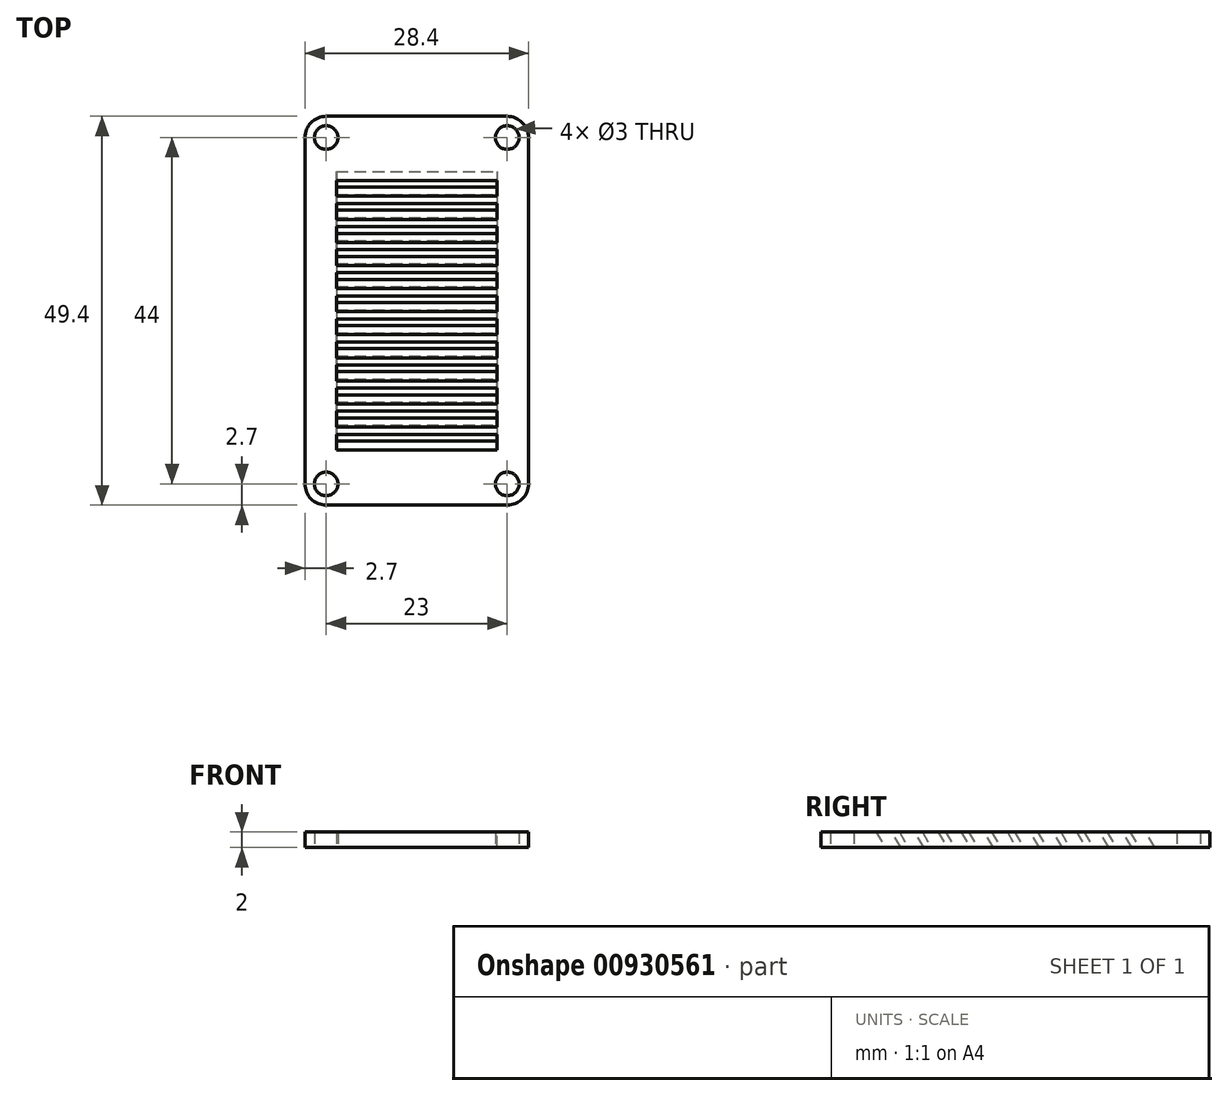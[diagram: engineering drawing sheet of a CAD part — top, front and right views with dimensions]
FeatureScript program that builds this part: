
annotation { "Feature Type Name" : "Feature", "Feature Type Description" : "" }
export const myFeature = defineFeature(function(context is Context, id is Id, definition is map)
    precondition{}
    {
        {
            var Q0;
            Q0=qCreatedBy(makeId("Top.planeOp"),FACE);
            var sketch = newSketch(context, id + "F0", { "sketchPlane" : qUnion([Q0])});
            skLineSegment(sketch, "E0", {"start": v(-14.5, 47) * mm, "end": v(-14.5, 3) * mm, "construction": true});
            skLineSegment(sketch, "E1", {"start": v(-11.5, 0) * mm, "end": v(11.5, 0) * mm, "construction": true});
            skLineSegment(sketch, "E2", {"start": v(14.5, 47) * mm, "end": v(14.5, 3) * mm, "construction": true});
            skLineSegment(sketch, "E3", {"start": v(-11.5, 50) * mm, "end": v(11.5, 50) * mm, "construction": true});
            skArc(sketch, "E4", {"start": v(-11.5, 50) * mm, "mid": v(-13.62, 49.12) * mm, "end": v(-14.5, 47) * mm, "construction": true});
            skArc(sketch, "E5", {"start": v(14.5, 47) * mm, "mid": v(13.62, 49.12) * mm, "end": v(11.5, 50) * mm, "construction": true});
            skArc(sketch, "E6", {"start": v(-14.5, 3) * mm, "mid": v(-13.62, 0.88) * mm, "end": v(-11.5, 0) * mm, "construction": true});
            skArc(sketch, "E7", {"start": v(11.5, 0) * mm, "mid": v(13.62, 0.88) * mm, "end": v(14.5, 3) * mm, "construction": true});
            skLineSegment(sketch, "E8", {"start": v(-14.2, 47) * mm, "end": v(-14.2, 3) * mm});
            skLineSegment(sketch, "E9", {"start": v(-11.5, 49.7) * mm, "end": v(11.5, 49.7) * mm});
            skLineSegment(sketch, "E10", {"start": v(14.2, 47) * mm, "end": v(14.2, 3) * mm});
            skLineSegment(sketch, "E11", {"start": v(-11.5, 0.3) * mm, "end": v(11.5, 0.3) * mm});
            skArc(sketch, "E12", {"start": v(-11.5, 49.7) * mm, "mid": v(-13.4, 48.9) * mm, "end": v(-14.2, 47) * mm});
            skArc(sketch, "E13", {"start": v(14.2, 47) * mm, "mid": v(13.4, 48.9) * mm, "end": v(11.5, 49.7) * mm});
            skArc(sketch, "E14", {"start": v(-14.2, 3) * mm, "mid": v(-13.4, 1.1) * mm, "end": v(-11.5, 0.3) * mm});
            skArc(sketch, "E15", {"start": v(11.5, 0.3) * mm, "mid": v(13.4, 1.1) * mm, "end": v(14.2, 3) * mm});
            skCircle(sketch, "E16", {"center": v(-11.5, 47) * mm, "radius": 1.5 * mm});
            skCircle(sketch, "E17", {"center": v(11.5, 47) * mm, "radius": 1.5 * mm});
            skCircle(sketch, "E18", {"center": v(-11.5, 3) * mm, "radius": 1.5 * mm});
            skCircle(sketch, "E19", {"center": v(11.5, 3) * mm, "radius": 1.5 * mm});
            skLineSegment(sketch, "E20.bottom", {"start": v(-10.2, 42.7) * mm, "end": v(10.2, 42.7) * mm});
            skLineSegment(sketch, "E20.top", {"start": v(-10.2, 7.3) * mm, "end": v(10.2, 7.3) * mm});
            skLineSegment(sketch, "E20.left", {"start": v(-10.2, 42.7) * mm, "end": v(-10.2, 7.3) * mm});
            skLineSegment(sketch, "E20.right", {"start": v(10.2, 42.7) * mm, "end": v(10.2, 7.3) * mm});
            skSolve(sketch);
        }
        {
            var Q0;
            Q0=qSketchRegion(id+"F0",true);
            extrude(context, id + "F1", {"entities" : qUnion([Q0]), "depth" : 2 * mm, "offsetDistance" : 25 * mm});
        }
        {
            var Q0;
            Q0=makeQuery(id+"F1.opExtrude","SWEPT_FACE",FACE,{"disambiguationData":[OSD([sQuery(id+"F0.wireOp",EDGE,"E20.right")])]});
            var sketch = newSketch(context, id + "F2", { "sketchPlane" : qUnion([Q0])});
            skLineSegment(sketch, "E21", {"start": v(-42.7, 1) * mm, "end": v(-7.3, 1) * mm, "construction": true});
            skLineSegment(sketch, "E22", {"start": v(-25, 2) * mm, "end": v(-25, 0) * mm, "construction": true});
            skLineSegment(sketch, "E23", {"start": v(-24.88, 2) * mm, "end": v(-23.96, 2) * mm});
            skLineSegment(sketch, "E24", {"start": v(-23.96, 2) * mm, "end": v(-25.12, 0) * mm});
            skLineSegment(sketch, "E25", {"start": v(-25.12, 0) * mm, "end": v(-26.04, 0) * mm});
            skLineSegment(sketch, "E26", {"start": v(-26.04, 0) * mm, "end": v(-24.88, 2) * mm});
            skLineSegment(sketch, "E27", {"start": v(-25, 2) * mm, "end": v(-24.88, 2) * mm, "construction": true});
            skLineSegment(sketch, "E28", {"start": v(-25, 0) * mm, "end": v(-25.12, 0) * mm, "construction": true});
            skLineSegment(sketch, "E29", {"start": v(-21.95, 2) * mm, "end": v(-23.1, 0) * mm});
            skLineSegment(sketch, "E30", {"start": v(-23.1, 0) * mm, "end": v(-22.18, 0) * mm});
            skLineSegment(sketch, "E31", {"start": v(-22.18, 0) * mm, "end": v(-21.03, 2) * mm});
            skLineSegment(sketch, "E32", {"start": v(-21.03, 2) * mm, "end": v(-21.95, 2) * mm});
            skLineSegment(sketch, "E33", {"start": v(-19.02, 2) * mm, "end": v(-20.18, 0) * mm});
            skLineSegment(sketch, "E34", {"start": v(-20.18, 0) * mm, "end": v(-19.25, 0) * mm});
            skLineSegment(sketch, "E35", {"start": v(-19.25, 0) * mm, "end": v(-18.1, 2) * mm});
            skLineSegment(sketch, "E36", {"start": v(-18.1, 2) * mm, "end": v(-19.02, 2) * mm});
            skLineSegment(sketch, "E37", {"start": v(-16.1, 2) * mm, "end": v(-15.17, 2) * mm});
            skLineSegment(sketch, "E38", {"start": v(-15.17, 2) * mm, "end": v(-16.32, 0) * mm});
            skLineSegment(sketch, "E39", {"start": v(-16.32, 0) * mm, "end": v(-17.25, 0) * mm});
            skLineSegment(sketch, "E40", {"start": v(-17.25, 0) * mm, "end": v(-16.1, 2) * mm});
            skLineSegment(sketch, "E41", {"start": v(-13.16, 2) * mm, "end": v(-14.32, 0) * mm});
            skLineSegment(sketch, "E42", {"start": v(-14.32, 0) * mm, "end": v(-13.4, 0) * mm});
            skLineSegment(sketch, "E43", {"start": v(-13.4, 0) * mm, "end": v(-12.24, 2) * mm});
            skLineSegment(sketch, "E44", {"start": v(-12.24, 2) * mm, "end": v(-13.16, 2) * mm});
            skLineSegment(sketch, "E45", {"start": v(-10.23, 2) * mm, "end": v(-11.39, 0) * mm});
            skLineSegment(sketch, "E46", {"start": v(-11.39, 0) * mm, "end": v(-10.46, 0) * mm});
            skLineSegment(sketch, "E47", {"start": v(-10.46, 0) * mm, "end": v(-9.3, 2) * mm});
            skLineSegment(sketch, "E48", {"start": v(-9.3, 2) * mm, "end": v(-10.23, 2) * mm});
            skLineSegment(sketch, "E49", {"start": v(-7.3, 2) * mm, "end": v(-8.45, 0) * mm});
            skLineSegment(sketch, "E50", {"start": v(-8.45, 0) * mm, "end": v(-7.3, 0) * mm});
            skLineSegment(sketch, "E51", {"start": v(-23.96, 2) * mm, "end": v(-22.46, 1.13) * mm, "construction": true});
            skLineSegment(sketch, "E52", {"start": v(-21.03, 2) * mm, "end": v(-19.52, 1.13) * mm, "construction": true});
            skLineSegment(sketch, "E53", {"start": v(-18.1, 2) * mm, "end": v(-16.6, 1.13) * mm, "construction": true});
            skLineSegment(sketch, "E54", {"start": v(-15.17, 2) * mm, "end": v(-13.66, 1.13) * mm, "construction": true});
            skLineSegment(sketch, "E55", {"start": v(-12.24, 2) * mm, "end": v(-10.73, 1.13) * mm, "construction": true});
            skLineSegment(sketch, "E56", {"start": v(-9.3, 2) * mm, "end": v(-7.8, 1.13) * mm, "construction": true});
            skLineSegment(sketch, "E57", {"start": v(-7.3, 0) * mm, "end": v(-7.3, 2) * mm});
            skLineSegment(sketch, "E58", {"start": v(-26.9, 2) * mm, "end": v(-28.05, 0) * mm});
            skLineSegment(sketch, "E59", {"start": v(-28.05, 0) * mm, "end": v(-28.97, 0) * mm});
            skLineSegment(sketch, "E60", {"start": v(-28.97, 0) * mm, "end": v(-27.82, 2) * mm});
            skLineSegment(sketch, "E61", {"start": v(-27.82, 2) * mm, "end": v(-26.9, 2) * mm});
            skLineSegment(sketch, "E62", {"start": v(-29.82, 2) * mm, "end": v(-30.98, 0) * mm});
            skLineSegment(sketch, "E63", {"start": v(-30.98, 0) * mm, "end": v(-31.9, 0) * mm});
            skLineSegment(sketch, "E64", {"start": v(-31.9, 0) * mm, "end": v(-30.75, 2) * mm});
            skLineSegment(sketch, "E65", {"start": v(-30.75, 2) * mm, "end": v(-29.82, 2) * mm});
            skLineSegment(sketch, "E66", {"start": v(-32.75, 2) * mm, "end": v(-33.68, 2) * mm});
            skLineSegment(sketch, "E67", {"start": v(-33.68, 2) * mm, "end": v(-34.83, 0) * mm});
            skLineSegment(sketch, "E68", {"start": v(-34.83, 0) * mm, "end": v(-33.9, 0) * mm});
            skLineSegment(sketch, "E69", {"start": v(-33.9, 0) * mm, "end": v(-32.75, 2) * mm});
            skLineSegment(sketch, "E70", {"start": v(-35.68, 2) * mm, "end": v(-36.6, 2) * mm});
            skLineSegment(sketch, "E71", {"start": v(-36.6, 2) * mm, "end": v(-37.76, 0) * mm});
            skLineSegment(sketch, "E72", {"start": v(-37.76, 0) * mm, "end": v(-36.84, 0) * mm});
            skLineSegment(sketch, "E73", {"start": v(-36.84, 0) * mm, "end": v(-35.68, 2) * mm});
            skLineSegment(sketch, "E74", {"start": v(-38.61, 2) * mm, "end": v(-39.54, 2) * mm});
            skLineSegment(sketch, "E75", {"start": v(-39.54, 2) * mm, "end": v(-40.7, 0) * mm});
            skLineSegment(sketch, "E76", {"start": v(-40.7, 0) * mm, "end": v(-39.77, 0) * mm});
            skLineSegment(sketch, "E77", {"start": v(-39.77, 0) * mm, "end": v(-38.61, 2) * mm});
            skLineSegment(sketch, "E78", {"start": v(-26.9, 2) * mm, "end": v(-25.39, 1.13) * mm, "construction": true});
            skLineSegment(sketch, "E79", {"start": v(-29.82, 2) * mm, "end": v(-28.32, 1.13) * mm, "construction": true});
            skLineSegment(sketch, "E80", {"start": v(-32.75, 2) * mm, "end": v(-31.25, 1.13) * mm, "construction": true});
            skLineSegment(sketch, "E81", {"start": v(-35.68, 2) * mm, "end": v(-34.18, 1.13) * mm, "construction": true});
            skLineSegment(sketch, "E82", {"start": v(-38.61, 2) * mm, "end": v(-37.1, 1.13) * mm, "construction": true});
            skLineSegment(sketch, "E83", {"start": v(-42.7, 0) * mm, "end": v(-41.55, 2) * mm});
            skLineSegment(sketch, "E84", {"start": v(-41.55, 2) * mm, "end": v(-42.7, 2) * mm});
            skLineSegment(sketch, "E85", {"start": v(-42.7, 2) * mm, "end": v(-42.7, 0) * mm});
            skSolve(sketch);
        }
        {
            var Q0;
            Q0=qSketchRegion(id+"F2",true);
            extrude(context, id + "F3", {"entities" : qUnion([Q0]), "operationType" : NewBodyOperationType.ADD, "endBound" : BoundingType.UP_TO_NEXT, "depth" : 25 * mm, "offsetDistance" : 25 * mm});
        }
    });
